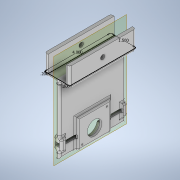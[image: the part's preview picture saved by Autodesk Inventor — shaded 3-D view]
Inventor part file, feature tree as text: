
AUTODESK INVENTOR PART (.ipt)
format: ipt  version: 2020 (Build 240168000, 168)  size: 437,248 bytes
history: native  units: in
note: dims shown in document units (in); Inventor stores cm internally (conversion verified against a paired STEP export)
features: sketch x7, extrude x6, fillet x6, hole x2, plane x1, mirror x1
ambient origin geometry x8: Origin, YZ Plane, XZ Plane, XY Plane, X Axis, Y Axis, Z Axis, Center Point
bodies: Solid1 (feature_tree)
feature tree (23):
  sketch  "Sketch1"  dims[d0=1.5in d1=4.0in]
  extrude  "Extrusion1"  Depth=4.0in
  extrude  "Extrusion2"  Depth=0.2in
  hole  "Hole1"  [1 undecoded]
  extrude  "Extrusion3"  Depth=0.25in TaperAngle=0.0deg
  extrude  "Extrusion4"  Depth=1.1024in
  extrude  "Extrusion5"  Depth=0.125in TaperAngle=0.0deg
  plane  "Work Plane1"
  mirror  "Mirror1"
  extrude  "Extrusion6"  Depth=0.25in
  hole  "Hole2"  [1 undecoded]
  fillet  "Fillet1"  Radius=0.25in
  fillet  "Fillet2"  Radius=0.25in
  fillet  "Fillet3"  Radius=0.125in
  fillet  "Fillet4"  Radius=1.0in
  fillet  "Fillet5"  Radius=1.0in
  fillet  "Fillet6"  Radius=1.75in
  sketch  "Sketch2"  dims[d2=0.2in d3=0.2in]
  sketch  "Sketch3"  dims[d4=1.0in d5=0.0in d6=0.2in d7=0.0in]
  sketch  "Sketch4"  dims[d8=0.5in]
  sketch  "Sketch5"  dims[d9=0.266in d10=0.75in d11=0.438in d12=0.25in d13=0.5635in d14=1.0in d15=0.8108in d16=4.0in d17=0.0in]
  sketch  "Sketch6"  dims[d18=0.75in d19=1.1024in]
  sketch  "Sketch7"  dims[d20=0.1969in d21=4.0in d22=0.0in d23=0.25in d24=0.25in d25=0.25in d26=0.25in d27=0.125in d28=0.0in d29=1.0in d30=1.0in d31=1.75in d32=0.875in d33=0.125in d34=0.0in d35=0.25in d36=0.25in d37=0.25in d38=0.25in d39=0.089in d40=0.75in d41=0.119in d42=0.25in d43=0.5635in d44=0.5in d45=0.8108in d46=0.125in d47=0.125in d48=0.125in d49=0.125in d50=0.125in d51=0.125in]
note: 2 required parameter values undecoded (feature->parameter linkage not recoverable at this tier; creation-order binding heuristic only, values carry confidence <= 0.55)
